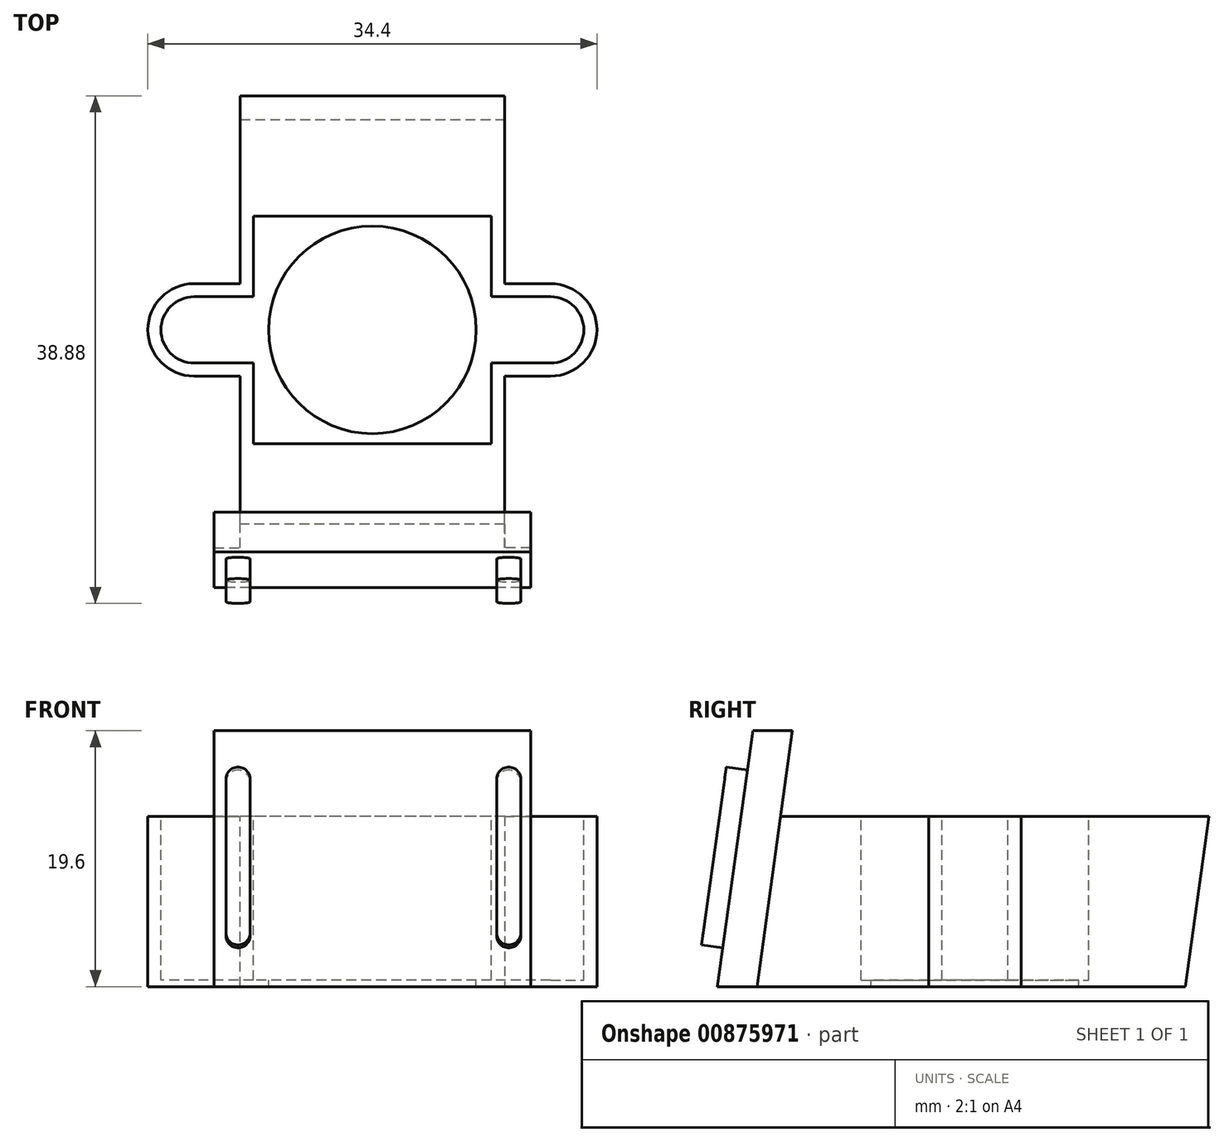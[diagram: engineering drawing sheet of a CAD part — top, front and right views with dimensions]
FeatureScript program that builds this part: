
annotation { "Feature Type Name" : "Feature", "Feature Type Description" : "" }
export const myFeature = defineFeature(function(context is Context, id is Id, definition is map)
    precondition{}
    {
        {
            var Q0;
            Q0=qCreatedBy(makeId("Top.planeOp"),FACE);
            var sketch = newSketch(context, id + "F0", { "sketchPlane" : qUnion([Q0])});
            skLineSegment(sketch, "E0.bottom", {"start": v(10.12, -9.72) * mm, "end": v(-10.12, -9.73) * mm});
            skLineSegment(sketch, "E0.top", {"start": v(10.12, 9.73) * mm, "end": v(-10.12, 9.72) * mm});
            skLineSegment(sketch, "E0.left", {"start": v(10.12, -9.72) * mm, "end": v(10.12, 9.73) * mm});
            skLineSegment(sketch, "E0.right", {"start": v(-10.12, -9.73) * mm, "end": v(-10.12, 9.72) * mm});
            skPoint(sketch, "E0.middle", {"position": v(0, 0) * mm});
            skCircle(sketch, "E1", {"center": v(-13.66, 0) * mm, "radius": 3.54 * mm});
            skCircle(sketch, "E2", {"center": v(13.66, 0) * mm, "radius": 3.54 * mm});
            skLineSegment(sketch, "E3.bottom", {"start": v(-13.66, 3.54) * mm, "end": v(13.66, 3.54) * mm});
            skLineSegment(sketch, "E3.top", {"start": v(-13.66, -3.54) * mm, "end": v(13.66, -3.54) * mm});
            skLineSegment(sketch, "E3.left", {"start": v(-13.66, 3.54) * mm, "end": v(-13.66, -3.54) * mm});
            skLineSegment(sketch, "E3.right", {"start": v(13.66, 3.54) * mm, "end": v(13.66, -3.54) * mm});
            skSolve(sketch);
        }
        {
            var Q0;
            Q0 = qSketchRegion(id + "F0", true);
            extrude(context, id + "F1", {"entities" : qUnion([Q0]), "depth" : 13.05 * mm, "offsetDistance" : 25 * mm});
        }
        {
            var Q0;
            Q0=makeQuery(id+"F1.opExtrude","CAP_FACE",FACE,{"disambiguationData":[OSD([sQuery(id+"F0.wireOp",EDGE,"E0.bottom"),sQuery(id+"F0.wireOp",EDGE,"E0.top"),sQuery(id+"F0.wireOp",EDGE,"E0.left"),sQuery(id+"F0.wireOp",EDGE,"E0.right"),sQuery(id+"F0.wireOp",EDGE,"E1"),sQuery(id+"F0.wireOp",EDGE,"E2"),sQuery(id+"F0.wireOp",EDGE,"oSXr4E67-9KMn-SXvF-eVTW-fJemWlPYfPIf.bottom"),sQuery(id+"F0.wireOp",EDGE,"oSXr4E67-9KMn-SXvF-eVTW-fJemWlPYfPIf.top")])],"isStart":false});
            var sketch = newSketch(context, id + "F2", { "sketchPlane" : qUnion([Q0])});
            skLineSegment(sketch, "E4.bottom", {"start": v(9.12, -8.72) * mm, "end": v(-9.12, -8.72) * mm});
            skLineSegment(sketch, "E4.top", {"start": v(9.12, 8.72) * mm, "end": v(-9.12, 8.72) * mm});
            skLineSegment(sketch, "E4.left", {"start": v(9.12, -8.72) * mm, "end": v(9.12, 8.72) * mm});
            skLineSegment(sketch, "E4.right", {"start": v(-9.12, -8.72) * mm, "end": v(-9.12, 8.72) * mm});
            skPoint(sketch, "E4.middle", {"position": v(0, 0) * mm});
            skSolve(sketch);
        }
        {
            var Q0;
            Q0=makeQuery(id+"F2.imprint","IMPRINT",FACE,{"disambiguationData":[TD([[makeQuery(id+"F2.imprint","IMPRINT",EDGE,{"derivedFrom":sQuery(id+"F2.wireOp",EDGE,"E4.bottom")}),-1.0]])]});
            extrude(context, id + "F3", {"entities" : qUnion([Q0]), "operationType" : NewBodyOperationType.REMOVE, "oppositeDirection" : true, "depth" : 12.55 * mm, "offsetDistance" : 25 * mm});
        }
        {
            var Q0;
            Q0=makeQuery(id+"F1.opExtrude","CAP_FACE",FACE,{"disambiguationData":[OSD([sQuery(id+"F0.wireOp",EDGE,"E0.bottom"),sQuery(id+"F0.wireOp",EDGE,"E0.top"),sQuery(id+"F0.wireOp",EDGE,"E0.left"),sQuery(id+"F0.wireOp",EDGE,"E0.right"),sQuery(id+"F0.wireOp",EDGE,"E1"),sQuery(id+"F0.wireOp",EDGE,"E2"),sQuery(id+"F0.wireOp",EDGE,"oSXr4E67-9KMn-SXvF-eVTW-fJemWlPYfPIf.bottom"),sQuery(id+"F0.wireOp",EDGE,"oSXr4E67-9KMn-SXvF-eVTW-fJemWlPYfPIf.top")])],"isStart":false});
            var sketch = newSketch(context, id + "F4", { "sketchPlane" : qUnion([Q0])});
            skCircle(sketch, "E5", {"center": v(-13.66, 0) * mm, "radius": 2.54 * mm});
            skCircle(sketch, "E6", {"center": v(13.66, 0) * mm, "radius": 2.54 * mm});
            skLineSegment(sketch, "E7.bottom", {"start": v(13.66, -2.54) * mm, "end": v(-13.66, -2.54) * mm});
            skLineSegment(sketch, "E7.top", {"start": v(13.66, 2.54) * mm, "end": v(-13.66, 2.54) * mm});
            skLineSegment(sketch, "E7.left", {"start": v(13.66, -2.54) * mm, "end": v(13.66, 2.54) * mm});
            skLineSegment(sketch, "E7.right", {"start": v(-13.66, -2.54) * mm, "end": v(-13.66, 2.54) * mm});
            skPoint(sketch, "E7.middle", {"position": v(0, 0) * mm});
            skSolve(sketch);
        }
        {
            var Q0;
            Q0 = qSketchRegion(id + "F4", true);
            extrude(context, id + "F5", {"entities" : qUnion([Q0]), "operationType" : NewBodyOperationType.REMOVE, "oppositeDirection" : true, "depth" : 12.55 * mm, "offsetDistance" : 25 * mm});
        }
        {
            var Q0;
            Q0=makeQuery(id+"F5.boolean.opBoolean","MERGE",FACE,{"derivedFrom":[makeQuery(id+"F3.boolean.opBoolean","COPY",FACE,{"derivedFrom":makeQuery(id+"F3.opExtrude","CAP_FACE",FACE,{"disambiguationData":[OSD([sQuery(id+"F2.wireOp",EDGE,"E4.bottom"),sQuery(id+"F2.wireOp",EDGE,"E4.top"),sQuery(id+"F2.wireOp",EDGE,"E4.left"),sQuery(id+"F2.wireOp",EDGE,"E4.right")])],"isStart":false})})],"fromTools":[makeQuery(id+"F5.opExtrude","CAP_FACE",FACE,{"disambiguationData":[OSD([sQuery(id+"F4.wireOp",EDGE,"E5"),sQuery(id+"F4.wireOp",EDGE,"E6"),sQuery(id+"F4.wireOp",EDGE,"E7.bottom"),sQuery(id+"F4.wireOp",EDGE,"E7.top")])],"isStart":false})]});
            var sketch = newSketch(context, id + "F6", { "sketchPlane" : qUnion([Q0])});
            skCircle(sketch, "E8", {"center": v(0, 0) * mm, "radius": 7.95 * mm});
            skSolve(sketch);
        }
        {
            var Q0;
            Q0 = qSketchRegion(id + "F6", true);
            extrude(context, id + "F7", {"entities" : qUnion([Q0]), "operationType" : NewBodyOperationType.REMOVE, "endBound" : BoundingType.THROUGH_ALL, "oppositeDirection" : true, "depth" : 25 * mm, "offsetDistance" : 25 * mm});
        }
        {
            var Q0;
            Q0=makeQuery(id+"F1.opExtrude","SWEPT_FACE",FACE,{"disambiguationData":[OSD([sQuery(id+"F0.wireOp",EDGE,"E0.bottom")])]});
            var sketch = newSketch(context, id + "F8", { "sketchPlane" : qUnion([Q0])});
            skLineSegment(sketch, "E9.bottom", {"start": v(-10.12, 13.05) * mm, "end": v(10.11, 13.05) * mm});
            skLineSegment(sketch, "E9.top", {"start": v(-10.12, 0) * mm, "end": v(10.11, 0) * mm});
            skLineSegment(sketch, "E9.left", {"start": v(-10.12, 13.05) * mm, "end": v(-10.12, 0) * mm});
            skLineSegment(sketch, "E9.right", {"start": v(10.11, 13.05) * mm, "end": v(10.11, 0) * mm});
            skSolve(sketch);
        }
        {
            var Q0;
            Q0 = qSketchRegion(id + "F8", true);
            extrude(context, id + "F9", {"entities" : qUnion([Q0]), "operationType" : NewBodyOperationType.ADD, "depth" : 10 * mm, "offsetDistance" : 25 * mm});
        }
        {
            var Q0;
            Q0=makeQuery(id+"F9.boolean.opBoolean","MERGE",FACE,{"derivedFrom":[makeQuery(id+"F1.opExtrude","CAP_FACE",FACE,{"disambiguationData":[OSD([sQuery(id+"F0.wireOp",EDGE,"E0.bottom"),sQuery(id+"F0.wireOp",EDGE,"E0.top"),sQuery(id+"F0.wireOp",EDGE,"E0.left"),sQuery(id+"F0.wireOp",EDGE,"E0.right"),sQuery(id+"F0.wireOp",EDGE,"E1"),sQuery(id+"F0.wireOp",EDGE,"E2"),sQuery(id+"F0.wireOp",EDGE,"E3.bottom"),sQuery(id+"F0.wireOp",EDGE,"E3.top")])],"isStart":false}),makeQuery(id+"F9.opExtrude","SWEPT_FACE",FACE,{"disambiguationData":[OSD([sQuery(id+"F8.wireOp",EDGE,"E9.bottom")])]})]});
            var sketch = newSketch(context, id + "F10", { "sketchPlane" : qUnion([Q0])});
            skLineSegment(sketch, "E10.bottom", {"start": v(-10.11, -19.72) * mm, "end": v(10.11, -19.72) * mm});
            skLineSegment(sketch, "E10.top", {"start": v(-10.11, -9.76) * mm, "end": v(10.11, -9.76) * mm});
            skLineSegment(sketch, "E10.left", {"start": v(-10.11, -19.72) * mm, "end": v(-10.11, -9.76) * mm});
            skLineSegment(sketch, "E10.right", {"start": v(10.12, -19.72) * mm, "end": v(10.12, -9.76) * mm});
            skSolve(sketch);
        }
        {
            var Q0;
            Q0 = qSketchRegion(id + "F10", true);
            extrude(context, id + "F11", {"entities" : qUnion([Q0]), "operationType" : NewBodyOperationType.ADD, "depth" : 25 * mm, "offsetDistance" : 25 * mm});
        }
        {
            var Q0;
            {var subQ0=sQuery(id+"F0.wireOp",EDGE,"E0.right");Q0=makeQuery(id+"F11.boolean.opBoolean","MERGE",FACE,{"derivedFrom":[makeQuery(id+"F9.boolean.opBoolean","MERGE",FACE,{"derivedFrom":[makeQuery(id+"F1.opExtrude","SWEPT_FACE",FACE,{"disambiguationData":[OSD([subQ0]),TDD([makeQuery(id+"F0.imprint","IMPRINT",EDGE,{"disambiguationData":[TD([[makeQuery(id+"F0.imprint","INTERSECT",VERTEX,{"derivedFrom":[sQuery(id+"F0.wireOp",EDGE,"E0.bottom"),subQ0]}),-1.0]])],"derivedFrom":subQ0})])]}),makeQuery(id+"F9.opExtrude","SWEPT_FACE",FACE,{"disambiguationData":[OSD([sQuery(id+"F8.wireOp",EDGE,"E9.left")])]})]}),makeQuery(id+"F11.opExtrude","SWEPT_FACE",FACE,{"disambiguationData":[OSD([sQuery(id+"F10.wireOp",EDGE,"E10.left")])]})]});}
            var sketch = newSketch(context, id + "F12", { "sketchPlane" : qUnion([Q0])});
            skLineSegment(sketch, "E11", {"start": v(14.42, 38.05) * mm, "end": v(19.72, 0) * mm});
            skLineSegment(sketch, "E12", {"start": v(19.72, 0) * mm, "end": v(19.72, 38.05) * mm});
            skLineSegment(sketch, "E13", {"start": v(19.72, 38.05) * mm, "end": v(14.42, 38.05) * mm});
            skSolve(sketch);
        }
        {
            var Q0;
            Q0 = qSketchRegion(id + "F12", true);
            extrude(context, id + "F13", {"entities" : qUnion([Q0]), "operationType" : NewBodyOperationType.REMOVE, "endBound" : BoundingType.THROUGH_ALL, "oppositeDirection" : true, "depth" : 25 * mm, "offsetDistance" : 25 * mm});
        }
        {
            var Q0;
            {var subQ0=sQuery(id+"F0.wireOp",EDGE,"E0.right");Q0=makeQuery(id+"F11.boolean.opBoolean","MERGE",FACE,{"derivedFrom":[makeQuery(id+"F9.boolean.opBoolean","MERGE",FACE,{"derivedFrom":[makeQuery(id+"F1.opExtrude","SWEPT_FACE",FACE,{"disambiguationData":[OSD([subQ0]),TDD([makeQuery(id+"F0.imprint","IMPRINT",EDGE,{"disambiguationData":[TD([[makeQuery(id+"F0.imprint","INTERSECT",VERTEX,{"derivedFrom":[sQuery(id+"F0.wireOp",EDGE,"E0.bottom"),subQ0]}),-1.0]])],"derivedFrom":subQ0})])]}),makeQuery(id+"F9.opExtrude","SWEPT_FACE",FACE,{"disambiguationData":[OSD([sQuery(id+"F8.wireOp",EDGE,"E9.left")])]})]}),makeQuery(id+"F11.opExtrude","SWEPT_FACE",FACE,{"disambiguationData":[OSD([sQuery(id+"F10.wireOp",EDGE,"E10.left")])]})]});}
            var sketch = newSketch(context, id + "F14", { "sketchPlane" : qUnion([Q0])});
            skLineSegment(sketch, "E14", {"start": v(14.88, 13.05) * mm, "end": v(11.42, 38.05) * mm});
            skLineSegment(sketch, "E15", {"start": v(14.88, 13.05) * mm, "end": v(9.76, 13.05) * mm});
            skLineSegment(sketch, "E16", {"start": v(9.76, 13.05) * mm, "end": v(9.76, 38.05) * mm});
            skLineSegment(sketch, "E17", {"start": v(9.76, 38.05) * mm, "end": v(11.42, 38.05) * mm});
            skSolve(sketch);
        }
        {
            var Q0;
            Q0 = qSketchRegion(id + "F14", true);
            extrude(context, id + "F15", {"entities" : qUnion([Q0]), "operationType" : NewBodyOperationType.REMOVE, "endBound" : BoundingType.THROUGH_ALL, "oppositeDirection" : true, "depth" : 25 * mm, "offsetDistance" : 25 * mm});
        }
        {
            var Q0;
            {var subQ0=sQuery(id+"F0.wireOp",EDGE,"E0.left");Q0=makeQuery(id+"F11.boolean.opBoolean","MERGE",FACE,{"derivedFrom":[makeQuery(id+"F9.boolean.opBoolean","MERGE",FACE,{"derivedFrom":[makeQuery(id+"F1.opExtrude","SWEPT_FACE",FACE,{"disambiguationData":[OSD([subQ0]),TDD([makeQuery(id+"F0.imprint","IMPRINT",EDGE,{"disambiguationData":[TD([[makeQuery(id+"F0.imprint","INTERSECT",VERTEX,{"derivedFrom":[sQuery(id+"F0.wireOp",EDGE,"E0.bottom"),subQ0]}),-1.0]])],"derivedFrom":subQ0})])]}),makeQuery(id+"F9.opExtrude","SWEPT_FACE",FACE,{"disambiguationData":[OSD([sQuery(id+"F8.wireOp",EDGE,"E9.right")])]})]}),makeQuery(id+"F11.opExtrude","SWEPT_FACE",FACE,{"disambiguationData":[OSD([sQuery(id+"F10.wireOp",EDGE,"E10.right")])]})]});}
            var sketch = newSketch(context, id + "F16", { "sketchPlane" : qUnion([Q0])});
            skLineSegment(sketch, "E18", {"start": v(-14.42, 38.05) * mm, "end": v(-11.42, 38.05) * mm});
            skLineSegment(sketch, "E19", {"start": v(-11.42, 38.05) * mm, "end": v(-16.68, 0) * mm});
            skLineSegment(sketch, "E20", {"start": v(-16.68, 0) * mm, "end": v(-19.72, 0) * mm});
            skLineSegment(sketch, "E21", {"start": v(-19.72, 0) * mm, "end": v(-14.42, 38.05) * mm});
            skSolve(sketch);
        }
        {
            var Q0;
            Q0=makeQuery(id+"F1.opExtrude","SWEPT_FACE",FACE,{"disambiguationData":[OSD([sQuery(id+"F0.wireOp",EDGE,"E0.top")])]});
            var sketch = newSketch(context, id + "F17", { "sketchPlane" : qUnion([Q0])});
            skLineSegment(sketch, "E22.bottom", {"start": v(10.11, 0) * mm, "end": v(-10.12, 0) * mm});
            skLineSegment(sketch, "E22.top", {"start": v(10.11, 13.05) * mm, "end": v(-10.12, 13.05) * mm});
            skLineSegment(sketch, "E22.left", {"start": v(10.11, 0) * mm, "end": v(10.11, 13.05) * mm});
            skLineSegment(sketch, "E22.right", {"start": v(-10.12, 0) * mm, "end": v(-10.12, 13.05) * mm});
            skSolve(sketch);
        }
        {
            var Q0;
            Q0 = qSketchRegion(id + "F17", true);
            extrude(context, id + "F18", {"entities" : qUnion([Q0]), "operationType" : NewBodyOperationType.ADD, "depth" : 8.2 * mm, "offsetDistance" : 25 * mm});
        }
        {
            var Q0;
            {var subQ0=sQuery(id+"F0.wireOp",EDGE,"E0.left");Q0=makeQuery(id+"F18.boolean.opBoolean","MERGE",FACE,{"derivedFrom":[makeQuery(id+"F1.opExtrude","SWEPT_FACE",FACE,{"disambiguationData":[OSD([subQ0]),TDD([makeQuery(id+"F0.imprint","IMPRINT",EDGE,{"disambiguationData":[TD([[makeQuery(id+"F0.imprint","INTERSECT",VERTEX,{"derivedFrom":[sQuery(id+"F0.wireOp",EDGE,"E0.top"),subQ0]}),1.0]])],"derivedFrom":subQ0})])]}),makeQuery(id+"F18.opExtrude","SWEPT_FACE",FACE,{"disambiguationData":[OSD([sQuery(id+"F17.wireOp",EDGE,"E22.right")])]})]});}
            var sketch = newSketch(context, id + "F19", { "sketchPlane" : qUnion([Q0])});
            skLineSegment(sketch, "E23", {"start": v(17.93, 13.05) * mm, "end": v(16.12, 0) * mm});
            skLineSegment(sketch, "E24", {"start": v(16.12, 0) * mm, "end": v(17.93, 0) * mm});
            skLineSegment(sketch, "E25", {"start": v(17.93, 0) * mm, "end": v(17.93, 13.05) * mm});
            skSolve(sketch);
        }
        {
            var Q0;
            Q0 = qSketchRegion(id + "F19", true);
            extrude(context, id + "F20", {"entities" : qUnion([Q0]), "operationType" : NewBodyOperationType.REMOVE, "oppositeDirection" : true, "depth" : 25 * mm, "offsetDistance" : 25 * mm});
        }
        {
            var Q0;
            {var subQ0=sQuery(id+"F0.wireOp",EDGE,"E0.right");Q0=makeQuery(id+"F11.boolean.opBoolean","MERGE",FACE,{"derivedFrom":[makeQuery(id+"F9.boolean.opBoolean","MERGE",FACE,{"derivedFrom":[makeQuery(id+"F1.opExtrude","SWEPT_FACE",FACE,{"disambiguationData":[OSD([subQ0]),TDD([makeQuery(id+"F0.imprint","IMPRINT",EDGE,{"disambiguationData":[TD([[makeQuery(id+"F0.imprint","INTERSECT",VERTEX,{"derivedFrom":[sQuery(id+"F0.wireOp",EDGE,"E0.bottom"),subQ0]}),-1.0]])],"derivedFrom":subQ0})])]}),makeQuery(id+"F9.opExtrude","SWEPT_FACE",FACE,{"disambiguationData":[OSD([sQuery(id+"F8.wireOp",EDGE,"E9.left")])]})]}),makeQuery(id+"F11.opExtrude","SWEPT_FACE",FACE,{"disambiguationData":[OSD([sQuery(id+"F10.wireOp",EDGE,"E10.left")])]})]});}
            var sketch = newSketch(context, id + "F21", { "sketchPlane" : qUnion([Q0])});
            skLineSegment(sketch, "E26", {"start": v(14.42, 38.05) * mm, "end": v(19.72, 0) * mm});
            skLineSegment(sketch, "E27", {"start": v(11.42, 38.05) * mm, "end": v(16.68, 0) * mm});
            skLineSegment(sketch, "E28", {"start": v(16.68, 0) * mm, "end": v(19.72, 0) * mm});
            skLineSegment(sketch, "E29", {"start": v(14.42, 38.05) * mm, "end": v(11.42, 38.05) * mm});
            skSolve(sketch);
        }
        {
            var Q0;
            Q0 = qSketchRegion(id + "F21", true);
            extrude(context, id + "F22", {"entities" : qUnion([Q0]), "operationType" : NewBodyOperationType.ADD, "depth" : 2 * mm, "offsetDistance" : 25 * mm});
        }
        {
            var Q0;
            {var subQ6=sQuery(id+"F16.wireOp",EDGE,"E18");Q0=makeQuery(id+"F16.imprint","IMPRINT",FACE,{"disambiguationData":[TD([[makeQuery(id+"F16.imprint","IMPRINT",EDGE,{"derivedFrom":subQ6}),-1.0]])]});}
            extrude(context, id + "F23", {"entities" : qUnion([Q0]), "operationType" : NewBodyOperationType.ADD, "depth" : 2 * mm, "offsetDistance" : 25 * mm});
        }
        {
            var Q0;
            Q0=makeQuery(id+"F22.opExtrude","CAP_FACE",FACE,{"disambiguationData":[OSD([sQuery(id+"F21.wireOp",EDGE,"E26"),sQuery(id+"F21.wireOp",EDGE,"E27"),sQuery(id+"F21.wireOp",EDGE,"E28"),sQuery(id+"F21.wireOp",EDGE,"E29")])],"isStart":false});
            var sketch = newSketch(context, id + "F24", { "sketchPlane" : qUnion([Q0])});
            skLineSegment(sketch, "E30", {"start": v(13.97, 19.6) * mm, "end": v(17, 19.6) * mm});
            skSolve(sketch);
        }
        {
            var Q0;
            {var subQ0=sQuery(id+"F24.wireOp",EDGE,"E30");Q0=makeQuery(id+"F24.imprint","IMPRINT",FACE,{"disambiguationData":[TD([[makeQuery(id+"F24.imprint","IMPRINT",EDGE,{"derivedFrom":subQ0}),1.0]])]});}
            extrude(context, id + "F25", {"entities" : qUnion([Q0]), "operationType" : NewBodyOperationType.REMOVE, "endBound" : BoundingType.THROUGH_ALL, "oppositeDirection" : true, "depth" : 25 * mm, "offsetDistance" : 25 * mm});
        }
        {
            var Q0;
            Q0=makeQuery(id+"F23.boolean.opBoolean","MERGE",FACE,{"derivedFrom":[makeQuery(id+"F22.boolean.opBoolean","MERGE",FACE,{"derivedFrom":[makeQuery(id+"F13.boolean.opBoolean","COPY",FACE,{"derivedFrom":makeQuery(id+"F13.opExtrude","SWEPT_FACE",FACE,{"disambiguationData":[OSD([sQuery(id+"F12.wireOp",EDGE,"E11")])]})}),makeQuery(id+"F22.opExtrude","SWEPT_FACE",FACE,{"disambiguationData":[OSD([sQuery(id+"F21.wireOp",EDGE,"E26")])]})]}),makeQuery(id+"F23.opExtrude","SWEPT_FACE",FACE,{"disambiguationData":[OSD([sQuery(id+"F16.wireOp",EDGE,"E21")])]})]});
            var sketch = newSketch(context, id + "F26", { "sketchPlane" : qUnion([Q0])});
            skCircle(sketch, "E31", {"center": v(-10.3, 13.1) * mm, "radius": 0.93 * mm});
            skCircle(sketch, "E32", {"center": v(-10.29, 1.2) * mm, "radius": 0.93 * mm});
            skCircle(sketch, "E33", {"center": v(10.44, 13.1) * mm, "radius": 0.93 * mm});
            skCircle(sketch, "E34", {"center": v(10.44, 1.2) * mm, "radius": 0.93 * mm});
            skLineSegment(sketch, "E35", {"start": v(-11.22, 13.1) * mm, "end": v(-11.22, 1.2) * mm});
            skLineSegment(sketch, "E36", {"start": v(-9.36, 13.1) * mm, "end": v(-9.36, 1.2) * mm});
            skLineSegment(sketch, "E37", {"start": v(9.52, 13.1) * mm, "end": v(9.52, 1.2) * mm});
            skLineSegment(sketch, "E38", {"start": v(11.37, 13.1) * mm, "end": v(11.37, 1.2) * mm});
            skSolve(sketch);
        }
        {
            var Q0;
            Q0 = qSketchRegion(id + "F26", true);
            extrude(context, id + "F27", {"entities" : qUnion([Q0]), "operationType" : NewBodyOperationType.ADD, "depth" : 1.65 * mm, "offsetDistance" : 25 * mm});
        }
    });
